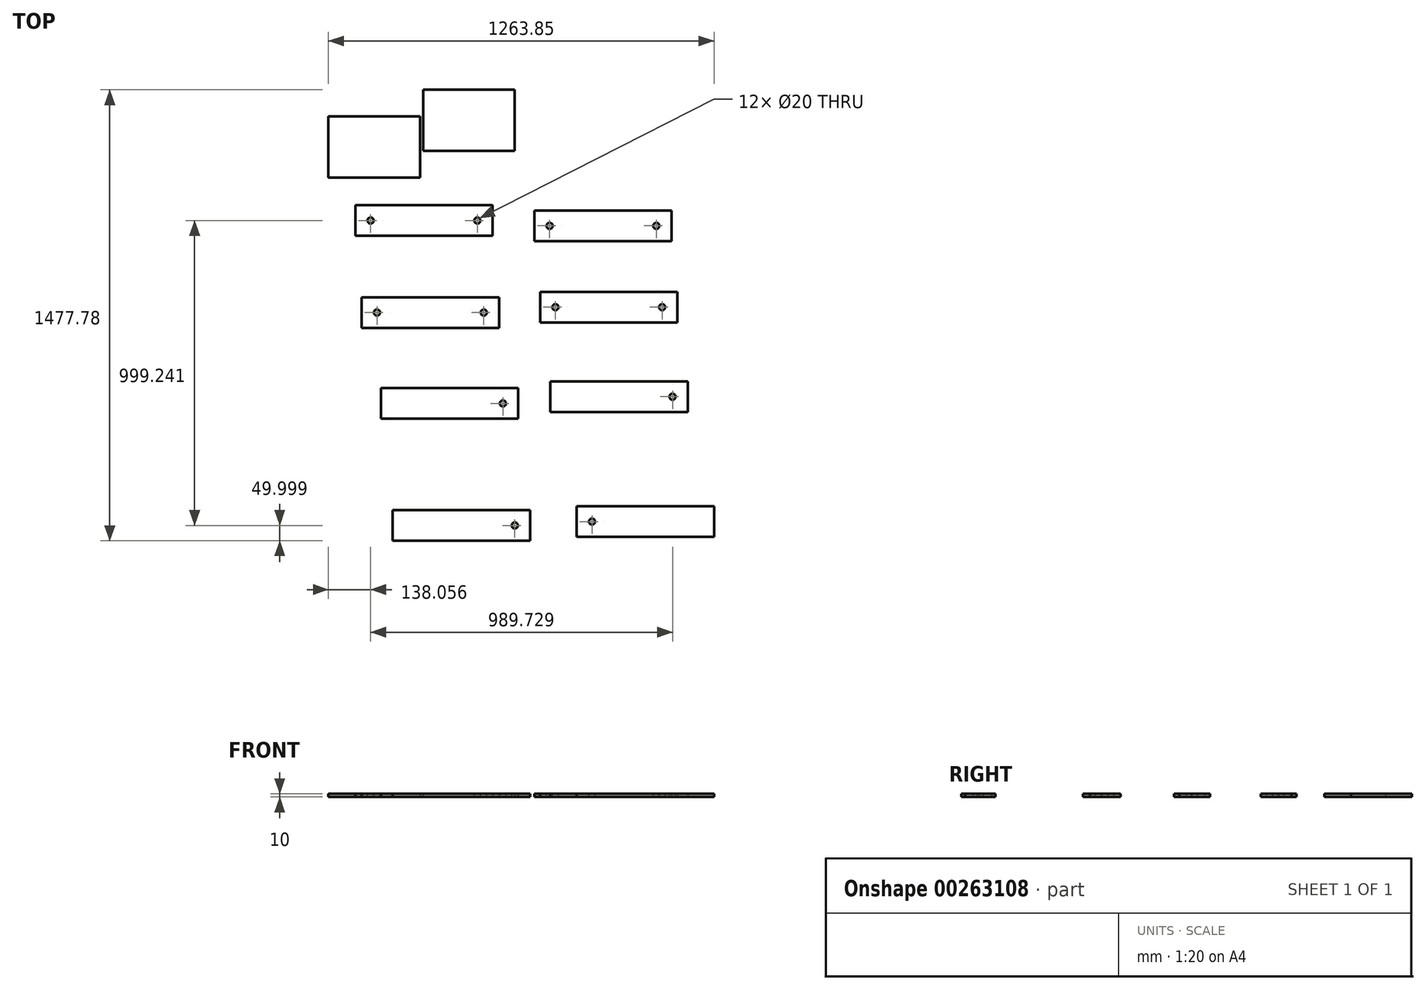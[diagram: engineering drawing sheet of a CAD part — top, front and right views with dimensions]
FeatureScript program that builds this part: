
annotation { "Feature Type Name" : "Feature", "Feature Type Description" : "" }
export const myFeature = defineFeature(function(context is Context, id is Id, definition is map)
    precondition{}
    {
        {
            var Q0;
            Q0=qCreatedBy(makeId("Top.planeOp"),FACE);
            var sketch = newSketch(context, id + "F0", { "sketchPlane" : qUnion([Q0])});
            skLineSegment(sketch, "E0.bottom", {"start": v(-280.83, 70.46) * mm, "end": v(19.17, 70.46) * mm});
            skLineSegment(sketch, "E0.top", {"start": v(-280.83, -129.54) * mm, "end": v(19.17, -129.54) * mm});
            skLineSegment(sketch, "E0.left", {"start": v(-280.83, 70.46) * mm, "end": v(-280.83, -129.54) * mm});
            skLineSegment(sketch, "E0.right", {"start": v(19.17, 70.46) * mm, "end": v(19.17, -129.54) * mm});
            skSolve(sketch);
        }
        {
            var Q0;
            Q0 = qSketchRegion(id + "F0", true);
            extrude(context, id + "F1", {"entities" : qUnion([Q0]), "depth" : 10 * mm});
        }
        {
            var Q0;
            Q0=qCreatedBy(makeId("Top.planeOp"),FACE);
            var sketch = newSketch(context, id + "F2", { "sketchPlane" : qUnion([Q0])});
            skLineSegment(sketch, "E1.bottom", {"start": v(30, 157.83) * mm, "end": v(330, 157.83) * mm});
            skLineSegment(sketch, "E1.top", {"start": v(30, -42.17) * mm, "end": v(330, -42.17) * mm});
            skLineSegment(sketch, "E1.left", {"start": v(30, 157.83) * mm, "end": v(30, -42.17) * mm});
            skLineSegment(sketch, "E1.right", {"start": v(330, 157.83) * mm, "end": v(330, -42.17) * mm});
            skSolve(sketch);
        }
        {
            var Q0;
            Q0 = qSketchRegion(id + "F2", true);
            extrude(context, id + "F3", {"entities" : qUnion([Q0]), "depth" : 10 * mm});
        }
        {
            var Q0;
            Q0=qCreatedBy(makeId("Top.planeOp"),FACE);
            var sketch = newSketch(context, id + "F4", { "sketchPlane" : qUnion([Q0])});
            skLineSegment(sketch, "E2.bottom", {"start": v(-192.77, -220.71) * mm, "end": v(257.23, -220.71) * mm});
            skLineSegment(sketch, "E2.top", {"start": v(-192.77, -320.71) * mm, "end": v(257.23, -320.71) * mm});
            skLineSegment(sketch, "E2.left", {"start": v(-192.77, -220.71) * mm, "end": v(-192.77, -320.71) * mm});
            skLineSegment(sketch, "E2.right", {"start": v(257.23, -220.71) * mm, "end": v(257.23, -320.71) * mm});
            skSolve(sketch);
        }
        {
            var Q0;
            Q0 = qSketchRegion(id + "F4", true);
            extrude(context, id + "F5", {"entities" : qUnion([Q0]), "depth" : 10 * mm});
        }
        {
            var Q0;
            Q0=qCreatedBy(makeId("Top.planeOp"),FACE);
            var sketch = newSketch(context, id + "F6", { "sketchPlane" : qUnion([Q0])});
            skLineSegment(sketch, "E3.bottom", {"start": v(-171.73, -522.18) * mm, "end": v(278.27, -522.18) * mm});
            skLineSegment(sketch, "E3.top", {"start": v(-171.73, -622.18) * mm, "end": v(278.27, -622.18) * mm});
            skLineSegment(sketch, "E3.left", {"start": v(-171.73, -522.18) * mm, "end": v(-171.73, -622.18) * mm});
            skLineSegment(sketch, "E3.right", {"start": v(278.27, -522.18) * mm, "end": v(278.27, -622.18) * mm});
            skSolve(sketch);
        }
        {
            var Q0;
            Q0 = qSketchRegion(id + "F6", true);
            extrude(context, id + "F7", {"entities" : qUnion([Q0]), "depth" : 10 * mm});
        }
        {
            var Q0;
            Q0=qCreatedBy(makeId("Top.planeOp"),FACE);
            var sketch = newSketch(context, id + "F8", { "sketchPlane" : qUnion([Q0])});
            skLineSegment(sketch, "E4.bottom", {"start": v(393.94, -238.13) * mm, "end": v(843.94, -238.13) * mm});
            skLineSegment(sketch, "E4.top", {"start": v(393.94, -338.13) * mm, "end": v(843.94, -338.13) * mm});
            skLineSegment(sketch, "E4.left", {"start": v(393.94, -238.13) * mm, "end": v(393.94, -338.13) * mm});
            skLineSegment(sketch, "E4.right", {"start": v(843.94, -238.13) * mm, "end": v(843.94, -338.13) * mm});
            skSolve(sketch);
        }
        {
            var Q0;
            Q0 = qSketchRegion(id + "F8", true);
            extrude(context, id + "F9", {"entities" : qUnion([Q0]), "depth" : 10 * mm});
        }
        {
            var Q0;
            Q0=qCreatedBy(makeId("Top.planeOp"),FACE);
            var sketch = newSketch(context, id + "F10", { "sketchPlane" : qUnion([Q0])});
            skLineSegment(sketch, "E5.bottom", {"start": v(412.97, -504.67) * mm, "end": v(862.97, -504.67) * mm});
            skLineSegment(sketch, "E5.top", {"start": v(412.97, -604.67) * mm, "end": v(862.97, -604.67) * mm});
            skLineSegment(sketch, "E5.left", {"start": v(412.97, -504.67) * mm, "end": v(412.97, -604.67) * mm});
            skLineSegment(sketch, "E5.right", {"start": v(862.97, -504.67) * mm, "end": v(862.97, -604.67) * mm});
            skSolve(sketch);
        }
        {
            var Q0;
            Q0 = qSketchRegion(id + "F10", true);
            extrude(context, id + "F11", {"entities" : qUnion([Q0]), "depth" : 10 * mm});
        }
        {
            var Q0;
            Q0=qCreatedBy(makeId("Top.planeOp"),FACE);
            var sketch = newSketch(context, id + "F12", { "sketchPlane" : qUnion([Q0])});
            skLineSegment(sketch, "E6.bottom", {"start": v(-109.08, -820.17) * mm, "end": v(340.92, -820.17) * mm});
            skLineSegment(sketch, "E6.top", {"start": v(-109.08, -920.17) * mm, "end": v(340.92, -920.17) * mm});
            skLineSegment(sketch, "E6.left", {"start": v(-109.08, -820.17) * mm, "end": v(-109.08, -920.17) * mm});
            skLineSegment(sketch, "E6.right", {"start": v(340.92, -820.17) * mm, "end": v(340.92, -920.17) * mm});
            skSolve(sketch);
        }
        {
            var Q0;
            Q0 = qSketchRegion(id + "F12", true);
            extrude(context, id + "F13", {"entities" : qUnion([Q0]), "depth" : 10 * mm});
        }
        {
            var Q0;
            Q0=qCreatedBy(makeId("Top.planeOp"),FACE);
            var sketch = newSketch(context, id + "F14", { "sketchPlane" : qUnion([Q0])});
            skLineSegment(sketch, "E7.bottom", {"start": v(446.95, -798.09) * mm, "end": v(896.95, -798.09) * mm});
            skLineSegment(sketch, "E7.top", {"start": v(446.95, -898.09) * mm, "end": v(896.95, -898.09) * mm});
            skLineSegment(sketch, "E7.left", {"start": v(446.95, -798.09) * mm, "end": v(446.95, -898.09) * mm});
            skLineSegment(sketch, "E7.right", {"start": v(896.95, -798.09) * mm, "end": v(896.95, -898.09) * mm});
            skSolve(sketch);
        }
        {
            var Q0;
            Q0 = qSketchRegion(id + "F14", true);
            extrude(context, id + "F15", {"entities" : qUnion([Q0]), "depth" : 10 * mm});
        }
        {
            var Q0;
            Q0=qCreatedBy(makeId("Top.planeOp"),FACE);
            var sketch = newSketch(context, id + "F16", { "sketchPlane" : qUnion([Q0])});
            skLineSegment(sketch, "E8.bottom", {"start": v(-69.93, -1219.95) * mm, "end": v(380.07, -1219.95) * mm});
            skLineSegment(sketch, "E8.top", {"start": v(-69.93, -1319.95) * mm, "end": v(380.07, -1319.95) * mm});
            skLineSegment(sketch, "E8.left", {"start": v(-69.93, -1219.95) * mm, "end": v(-69.93, -1319.95) * mm});
            skLineSegment(sketch, "E8.right", {"start": v(380.07, -1219.95) * mm, "end": v(380.07, -1319.95) * mm});
            skSolve(sketch);
        }
        {
            var Q0;
            Q0 = qSketchRegion(id + "F16", true);
            extrude(context, id + "F17", {"entities" : qUnion([Q0]), "depth" : 10 * mm});
        }
        {
            var Q0;
            Q0=qCreatedBy(makeId("Top.planeOp"),FACE);
            var sketch = newSketch(context, id + "F18", { "sketchPlane" : qUnion([Q0])});
            skLineSegment(sketch, "E9.bottom", {"start": v(533.02, -1207.5) * mm, "end": v(983.02, -1207.5) * mm});
            skLineSegment(sketch, "E9.top", {"start": v(533.02, -1307.5) * mm, "end": v(983.02, -1307.5) * mm});
            skLineSegment(sketch, "E9.left", {"start": v(533.02, -1207.5) * mm, "end": v(533.02, -1307.5) * mm});
            skLineSegment(sketch, "E9.right", {"start": v(983.02, -1207.5) * mm, "end": v(983.02, -1307.5) * mm});
            skSolve(sketch);
        }
        {
            var Q0;
            Q0 = qSketchRegion(id + "F18", true);
            extrude(context, id + "F19", {"entities" : qUnion([Q0]), "depth" : 10 * mm});
        }
        {
            var Q0;
            Q0=makeQuery(id+"F5.opExtrude","CAP_FACE",FACE,{"disambiguationData":[OSD([sQuery(id+"F4.wireOp",EDGE,"E2.bottom"),sQuery(id+"F4.wireOp",EDGE,"E2.top"),sQuery(id+"F4.wireOp",EDGE,"E2.left"),sQuery(id+"F4.wireOp",EDGE,"E2.right")])],"isStart":false});
            var sketch = newSketch(context, id + "F20", { "sketchPlane" : qUnion([Q0])});
            skCircle(sketch, "E10", {"center": v(-142.77, -270.71) * mm, "radius": 10 * mm});
            skSolve(sketch);
        }
        {
            var Q0;
            Q0 = qSketchRegion(id + "F20", true);
            extrude(context, id + "F21", {"entities" : qUnion([Q0]), "operationType" : NewBodyOperationType.REMOVE, "oppositeDirection" : true, "depth" : 25 * mm});
        }
        {
            var Q0;
            Q0=makeQuery(id+"F7.opExtrude","CAP_FACE",FACE,{"disambiguationData":[OSD([sQuery(id+"F6.wireOp",EDGE,"E3.bottom"),sQuery(id+"F6.wireOp",EDGE,"E3.top"),sQuery(id+"F6.wireOp",EDGE,"E3.left"),sQuery(id+"F6.wireOp",EDGE,"E3.right")])],"isStart":false});
            var sketch = newSketch(context, id + "F22", { "sketchPlane" : qUnion([Q0])});
            skCircle(sketch, "E11", {"center": v(-121.73, -572.18) * mm, "radius": 10 * mm});
            skSolve(sketch);
        }
        {
            var Q0;
            Q0 = qSketchRegion(id + "F22", true);
            extrude(context, id + "F23", {"entities" : qUnion([Q0]), "operationType" : NewBodyOperationType.REMOVE, "oppositeDirection" : true, "depth" : 25 * mm});
        }
        {
            var Q0;
            Q0=makeQuery(id+"F17.opExtrude","CAP_FACE",FACE,{"disambiguationData":[OSD([sQuery(id+"F16.wireOp",EDGE,"E8.bottom"),sQuery(id+"F16.wireOp",EDGE,"E8.top"),sQuery(id+"F16.wireOp",EDGE,"E8.left"),sQuery(id+"F16.wireOp",EDGE,"E8.right")])],"isStart":false});
            var sketch = newSketch(context, id + "F24", { "sketchPlane" : qUnion([Q0])});
            skCircle(sketch, "E12", {"center": v(330.07, -1269.95) * mm, "radius": 10 * mm});
            skSolve(sketch);
        }
        {
            var Q0;
            Q0 = qSketchRegion(id + "F24", true);
            extrude(context, id + "F25", {"entities" : qUnion([Q0]), "operationType" : NewBodyOperationType.REMOVE, "oppositeDirection" : true, "depth" : 25 * mm});
        }
        {
            var Q0;
            Q0=makeQuery(id+"F15.opExtrude","CAP_FACE",FACE,{"disambiguationData":[OSD([sQuery(id+"F14.wireOp",EDGE,"E7.bottom"),sQuery(id+"F14.wireOp",EDGE,"E7.top"),sQuery(id+"F14.wireOp",EDGE,"E7.left"),sQuery(id+"F14.wireOp",EDGE,"E7.right")])],"isStart":false});
            var sketch = newSketch(context, id + "F26", { "sketchPlane" : qUnion([Q0])});
            skCircle(sketch, "E13", {"center": v(846.95, -848.09) * mm, "radius": 10 * mm});
            skSolve(sketch);
        }
        {
            var Q0;
            Q0 = qSketchRegion(id + "F26", true);
            extrude(context, id + "F27", {"entities" : qUnion([Q0]), "operationType" : NewBodyOperationType.REMOVE, "oppositeDirection" : true, "depth" : 25 * mm});
        }
        {
            var Q0;
            Q0=makeQuery(id+"F5.opExtrude","CAP_FACE",FACE,{"disambiguationData":[OSD([sQuery(id+"F4.wireOp",EDGE,"E2.bottom"),sQuery(id+"F4.wireOp",EDGE,"E2.top"),sQuery(id+"F4.wireOp",EDGE,"E2.left"),sQuery(id+"F4.wireOp",EDGE,"E2.right")])],"isStart":false});
            var sketch = newSketch(context, id + "F28", { "sketchPlane" : qUnion([Q0])});
            skCircle(sketch, "E14", {"center": v(207.23, -270.71) * mm, "radius": 10 * mm});
            skPoint(sketch, "E14.centerSnap0", {"position": v(257.23, -270.71) * mm});
            skSolve(sketch);
        }
        {
            var Q0;
            Q0 = qSketchRegion(id + "F28", true);
            extrude(context, id + "F29", {"entities" : qUnion([Q0]), "operationType" : NewBodyOperationType.REMOVE, "oppositeDirection" : true, "depth" : 25 * mm});
        }
        {
            var Q0;
            Q0=makeQuery(id+"F9.opExtrude","CAP_FACE",FACE,{"disambiguationData":[OSD([sQuery(id+"F8.wireOp",EDGE,"E4.bottom"),sQuery(id+"F8.wireOp",EDGE,"E4.top"),sQuery(id+"F8.wireOp",EDGE,"E4.left"),sQuery(id+"F8.wireOp",EDGE,"E4.right")])],"isStart":false});
            var sketch = newSketch(context, id + "F30", { "sketchPlane" : qUnion([Q0])});
            skCircle(sketch, "E15", {"center": v(443.94, -288.13) * mm, "radius": 10 * mm});
            skSolve(sketch);
        }
        {
            var Q0;
            Q0 = qSketchRegion(id + "F30", true);
            extrude(context, id + "F31", {"entities" : qUnion([Q0]), "operationType" : NewBodyOperationType.REMOVE, "oppositeDirection" : true, "depth" : 25 * mm});
        }
        {
            var Q0;
            Q0=makeQuery(id+"F9.opExtrude","CAP_FACE",FACE,{"disambiguationData":[OSD([sQuery(id+"F8.wireOp",EDGE,"E4.bottom"),sQuery(id+"F8.wireOp",EDGE,"E4.top"),sQuery(id+"F8.wireOp",EDGE,"E4.left"),sQuery(id+"F8.wireOp",EDGE,"E4.right")])],"isStart":false});
            var sketch = newSketch(context, id + "F32", { "sketchPlane" : qUnion([Q0])});
            skCircle(sketch, "E16", {"center": v(793.94, -288.13) * mm, "radius": 10 * mm});
            skSolve(sketch);
        }
        {
            var Q0;
            Q0 = qSketchRegion(id + "F32", true);
            extrude(context, id + "F33", {"entities" : qUnion([Q0]), "operationType" : NewBodyOperationType.REMOVE, "oppositeDirection" : true, "depth" : 25 * mm});
        }
        {
            var Q0;
            Q0=makeQuery(id+"F7.opExtrude","CAP_FACE",FACE,{"disambiguationData":[OSD([sQuery(id+"F6.wireOp",EDGE,"E3.bottom"),sQuery(id+"F6.wireOp",EDGE,"E3.top"),sQuery(id+"F6.wireOp",EDGE,"E3.left"),sQuery(id+"F6.wireOp",EDGE,"E3.right")])],"isStart":false});
            var sketch = newSketch(context, id + "F34", { "sketchPlane" : qUnion([Q0])});
            skCircle(sketch, "E17", {"center": v(228.27, -572.18) * mm, "radius": 10 * mm});
            skSolve(sketch);
        }
        {
            var Q0;
            Q0 = qSketchRegion(id + "F34", true);
            extrude(context, id + "F35", {"entities" : qUnion([Q0]), "operationType" : NewBodyOperationType.REMOVE, "oppositeDirection" : true, "depth" : 25 * mm});
        }
        {
            var Q0;
            Q0=makeQuery(id+"F11.opExtrude","CAP_FACE",FACE,{"disambiguationData":[OSD([sQuery(id+"F10.wireOp",EDGE,"E5.bottom"),sQuery(id+"F10.wireOp",EDGE,"E5.top"),sQuery(id+"F10.wireOp",EDGE,"E5.left"),sQuery(id+"F10.wireOp",EDGE,"E5.right")])],"isStart":false});
            var sketch = newSketch(context, id + "F36", { "sketchPlane" : qUnion([Q0])});
            skCircle(sketch, "E18", {"center": v(462.97, -554.67) * mm, "radius": 10 * mm});
            skSolve(sketch);
        }
        {
            var Q0;
            Q0 = qSketchRegion(id + "F36", true);
            extrude(context, id + "F37", {"entities" : qUnion([Q0]), "operationType" : NewBodyOperationType.REMOVE, "oppositeDirection" : true, "depth" : 25 * mm});
        }
        {
            var Q0;
            Q0=makeQuery(id+"F11.opExtrude","CAP_FACE",FACE,{"disambiguationData":[OSD([sQuery(id+"F10.wireOp",EDGE,"E5.bottom"),sQuery(id+"F10.wireOp",EDGE,"E5.top"),sQuery(id+"F10.wireOp",EDGE,"E5.left"),sQuery(id+"F10.wireOp",EDGE,"E5.right")])],"isStart":false});
            var sketch = newSketch(context, id + "F38", { "sketchPlane" : qUnion([Q0])});
            skCircle(sketch, "E19", {"center": v(812.97, -554.67) * mm, "radius": 10 * mm});
            skSolve(sketch);
        }
        {
            var Q0;
            Q0 = qSketchRegion(id + "F38", true);
            extrude(context, id + "F39", {"entities" : qUnion([Q0]), "operationType" : NewBodyOperationType.REMOVE, "oppositeDirection" : true, "depth" : 25 * mm});
        }
        {
            var Q0;
            Q0=makeQuery(id+"F13.opExtrude","CAP_FACE",FACE,{"disambiguationData":[OSD([sQuery(id+"F12.wireOp",EDGE,"E6.bottom"),sQuery(id+"F12.wireOp",EDGE,"E6.top"),sQuery(id+"F12.wireOp",EDGE,"E6.left"),sQuery(id+"F12.wireOp",EDGE,"E6.right")])],"isStart":false});
            var sketch = newSketch(context, id + "F40", { "sketchPlane" : qUnion([Q0])});
            skCircle(sketch, "E20", {"center": v(290.92, -870.17) * mm, "radius": 10 * mm});
            skSolve(sketch);
        }
        {
            var Q0;
            Q0 = qSketchRegion(id + "F40", true);
            extrude(context, id + "F41", {"entities" : qUnion([Q0]), "operationType" : NewBodyOperationType.REMOVE, "oppositeDirection" : true, "depth" : 25 * mm});
        }
        {
            var Q0;
            Q0 = qSketchRegion(id + "F40", true);
            extrude(context, id + "F42", {"entities" : qUnion([Q0]), "operationType" : NewBodyOperationType.REMOVE, "oppositeDirection" : true, "depth" : 25 * mm});
        }
        {
            var Q0;
            Q0=makeQuery(id+"F19.opExtrude","CAP_FACE",FACE,{"disambiguationData":[OSD([sQuery(id+"F18.wireOp",EDGE,"E9.bottom"),sQuery(id+"F18.wireOp",EDGE,"E9.top"),sQuery(id+"F18.wireOp",EDGE,"E9.left"),sQuery(id+"F18.wireOp",EDGE,"E9.right")])],"isStart":false});
            var sketch = newSketch(context, id + "F43", { "sketchPlane" : qUnion([Q0])});
            skCircle(sketch, "E21", {"center": v(583.02, -1257.5) * mm, "radius": 10 * mm});
            skSolve(sketch);
        }
        {
            var Q0;
            Q0 = qSketchRegion(id + "F43", true);
            extrude(context, id + "F44", {"entities" : qUnion([Q0]), "operationType" : NewBodyOperationType.REMOVE, "oppositeDirection" : true, "depth" : 25 * mm});
        }
    });
